# Revit family: Woodfold-Accordion-Door-Family-Series-220
name_source: partatom
category: Doors
units: mm (PartAtom-declared; Revit-internal decimal feet)

## family parameters
Always vertical = Yes
Cut with Voids When Loaded = No
Host = Wall
Room Calculation Point = No
Shared = No

## types (2) — shared parameters
Description = Interior door
Frame Projection Ext. = 0' - 1"
Frame Projection Int. = 0' - 1"
Frame Visibility = No
Frame Width = 0' - 3"
Function = Interior
Height = 8' - 0"
Manufacturer = Woodfold Door
Model = Series 140
Panel Connector Material = Plastic - Formed Plastic
Panel Material = Woodfold - Cherry
Panel Offset from Top = 0' - 1 3/16"
Stack Dimension = 0' - 10 1/4"
Track Material = Plastic - Formed Plastic
Type Comments = Max Wd. 8'-0", Max Ht. 8'-0"
URL = www.woodfold.com
Wall Closure = By host
Width = 6' - 0"

## per-type parameters (varying)
| type | Recessed Track | Surface Mounted Track |
| 6'-0" x 8'-0" Surface Mounted | No | Yes |
| 6'-0" x 8'-0" Recessed Track | Yes | No |

## geometry (parser evidence)
native form markers: Sweep x20
no freeform markers — native parametric forms only
